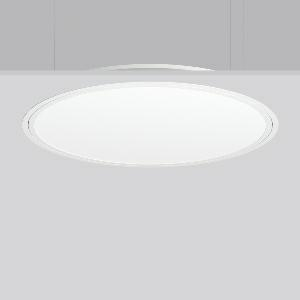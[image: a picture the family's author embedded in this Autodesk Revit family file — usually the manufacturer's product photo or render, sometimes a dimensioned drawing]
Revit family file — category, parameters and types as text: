
# Revit family: triona_round_e_312387_002_12_66c0
name_source: partatom
category: Lighting Fixtures
units: mm (PartAtom-declared; Revit-internal decimal feet)

## family parameters
Cut with Voids When Loaded = No
Host = Face
Light Source = No
Part Type = Normal
Room Calculation Point = No
Round Connector Dimension = Use Diameter
Shared = No

## types (1)
- TRIONA round E (1 x LED Modul 830, 8000 lm, 3000)
    Apparent Load = 80 VA
    CIE Flux Codes = 49 80 96 100 100
    Color Rendering = 80
    Color Temperature = 3000
    Default Elevation = 1800 mm
    Description = Series: TRIONA round
Decorative round LED recessed surface luminaire. Cover made of sheet steel, powder-coated. Frame made of aluminium, powder-coated. Recessed ring: aluminium extrusion profile, powder coated. Light emission through a diffuser: plastic, opal. Lightguide and diffuser made of non-yellowing plastic (PMMA). Lateral light emission (RZB SIDELITE technology) for above-average homogeneous light distribution. Suitable for installation in cavity ceilings. Tool-free mounting system thanks to the rocker arm mechanism (patent pending). Electronic ballast included. Very easy installation thanks to Plug+Play connection. 
Colour: traffic white, matt (RAL 9016)
Diameter: 889 mm
Height: 2 mm
Cut-out diameter: 866 mm
Recess height: 100 mm
Luminaire: recess height: 89 mm
Lamp: LED
Socket: without socket
Colour temperature: 3000K
Colour rendering index (CRI): 80
System power: 80 W
Rated luminous flux: 8000 lm
Luminous efficiency: 100 lm/W
Control gear: Converter, dimmable, DALI
Protection class: I
Type of protection: IP 40
    Height = 0 mm  [stored 0 ft]
    Lamp = 1 x LED Modul 830
    Lamp Light Flux = 8000 lm
    Lamp count = 1
    Length = 889 mm
    Lifetime = 50000 h
    Luminous efficacy = 100 lm/W
    Manufacturer = RZB
    ModVariant = No
    Model = 312387.002.12
    Mounting Place = Ceiling
    Mounting Type = Recessed
    Number of Poles = 1
    OnlyDefault = Yes
    Power Factor = 1
    Product Name = TRIONA round E
    Product group = Recessed modular luminaires
    ProductGroupID = 406
    Protection Class = Protection class I
    Protection Degree = IP 20
    RLX_Detail_Level = 1
    RLX_Emergency_Light_Flux = 0 lm
    RLX_Emergency_Type = 0
    RLX_Emergency_Type_DB = No
    RlxData = <blob elided: 37605 chars, md5=ee438e18>
    Socket = socket
    Standby Power = 0 W
    System Light Flux = 8000 lm
    System Power = 80 W
    Type Comments = Product without accessories
    Type Image = 312387.002.12.jpg
    URL = http://relux.com
    VarID = ---
    Voltage = 230 V
    Voltage Range = 220-240 V
    Weight = 0.00 kg
    Width = 0 mm  [stored 0 ft]

note: [stored X ft] marks values corroborated as IEEE doubles in the binary element streams (Revit-internal decimal feet)

## geometry (parser evidence)
native form markers: Blend x4, Sweep x10
no freeform markers — native parametric forms only
